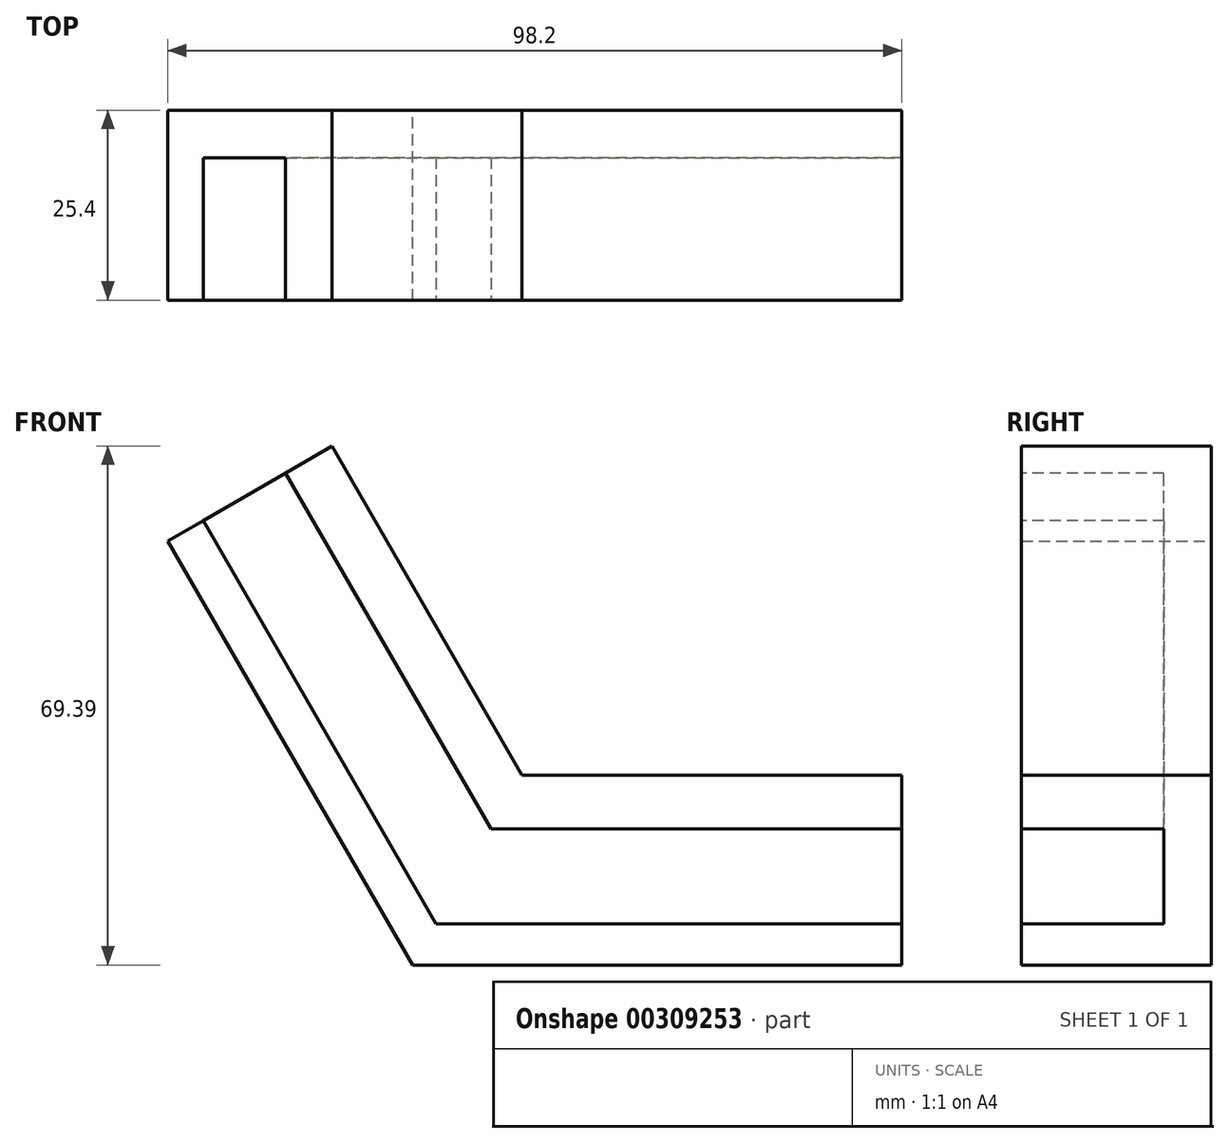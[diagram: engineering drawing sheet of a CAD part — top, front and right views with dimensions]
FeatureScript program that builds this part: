
annotation { "Feature Type Name" : "Feature", "Feature Type Description" : "" }
export const myFeature = defineFeature(function(context is Context, id is Id, definition is map)
    precondition{}
    {
        {
            var Q0;
            Q0=qCreatedBy(makeId("Front.planeOp"),FACE);
            var sketch = newSketch(context, id + "F0", { "sketchPlane" : qUnion([Q0])});
            skLineSegment(sketch, "E0", {"start": v(-47.4, 31.3) * mm, "end": v(-25.4, 44) * mm});
            skLineSegment(sketch, "E1", {"start": v(-25.4, 44) * mm, "end": v(0, 0) * mm});
            skLineSegment(sketch, "E2", {"start": v(0, 0) * mm, "end": v(50.8, 0) * mm});
            skLineSegment(sketch, "E3", {"start": v(50.8, 0) * mm, "end": v(50.8, -25.4) * mm});
            skLineSegment(sketch, "E4", {"start": v(50.8, -25.4) * mm, "end": v(-14.66, -25.4) * mm});
            skLineSegment(sketch, "E5", {"start": v(-14.66, -25.4) * mm, "end": v(-47.4, 31.3) * mm});
            skSolve(sketch);
        }
        {
            var Q0;
            Q0=makeQuery(id+"F0.imprint","IMPRINT",FACE,{"disambiguationData":[TD([[makeQuery(id+"F0.imprint","IMPRINT",EDGE,{"derivedFrom":sQuery(id+"F0.wireOp",EDGE,"E0")}),-1.0]])]});
            extrude(context, id + "F1", {"entities" : qUnion([Q0]), "depth" : 25.4 * mm});
        }
        {
            var Q0;
            Q0=makeQuery(id+"F1.opExtrude","CAP_FACE",FACE,{"disambiguationData":[OSD([sQuery(id+"F0.wireOp",EDGE,"E0"),sQuery(id+"F0.wireOp",EDGE,"E1"),sQuery(id+"F0.wireOp",EDGE,"E2"),sQuery(id+"F0.wireOp",EDGE,"E3"),sQuery(id+"F0.wireOp",EDGE,"E4"),sQuery(id+"F0.wireOp",EDGE,"E5")])],"isStart":false});
            var sketch = newSketch(context, id + "F2", { "sketchPlane" : qUnion([Q0])});
            skLineSegment(sketch, "E6", {"start": v(0, 0) * mm, "end": v(-14.66, -25.4) * mm, "construction": true});
            skLineSegment(sketch, "E7", {"start": v(-42.65, 34.04) * mm, "end": v(-11.5, -19.92) * mm});
            skLineSegment(sketch, "E8", {"start": v(-11.5, -19.92) * mm, "end": v(50.8, -19.92) * mm});
            skLineSegment(sketch, "E9", {"start": v(50.8, -19.92) * mm, "end": v(50.8, -7.22) * mm});
            skLineSegment(sketch, "E10", {"start": v(50.8, -7.22) * mm, "end": v(-4.17, -7.22) * mm});
            skLineSegment(sketch, "E11", {"start": v(-4.17, -7.22) * mm, "end": v(-31.65, 40.39) * mm});
            skLineSegment(sketch, "E12", {"start": v(-31.65, 40.39) * mm, "end": v(-42.65, 34.04) * mm});
            skSolve(sketch);
        }
        {
            var Q0;
            Q0 = qSketchRegion(id + "F2", true);
            extrude(context, id + "F3", {"entities" : qUnion([Q0]), "operationType" : NewBodyOperationType.REMOVE, "oppositeDirection" : true, "depth" : 19.05 * mm});
        }
    });
